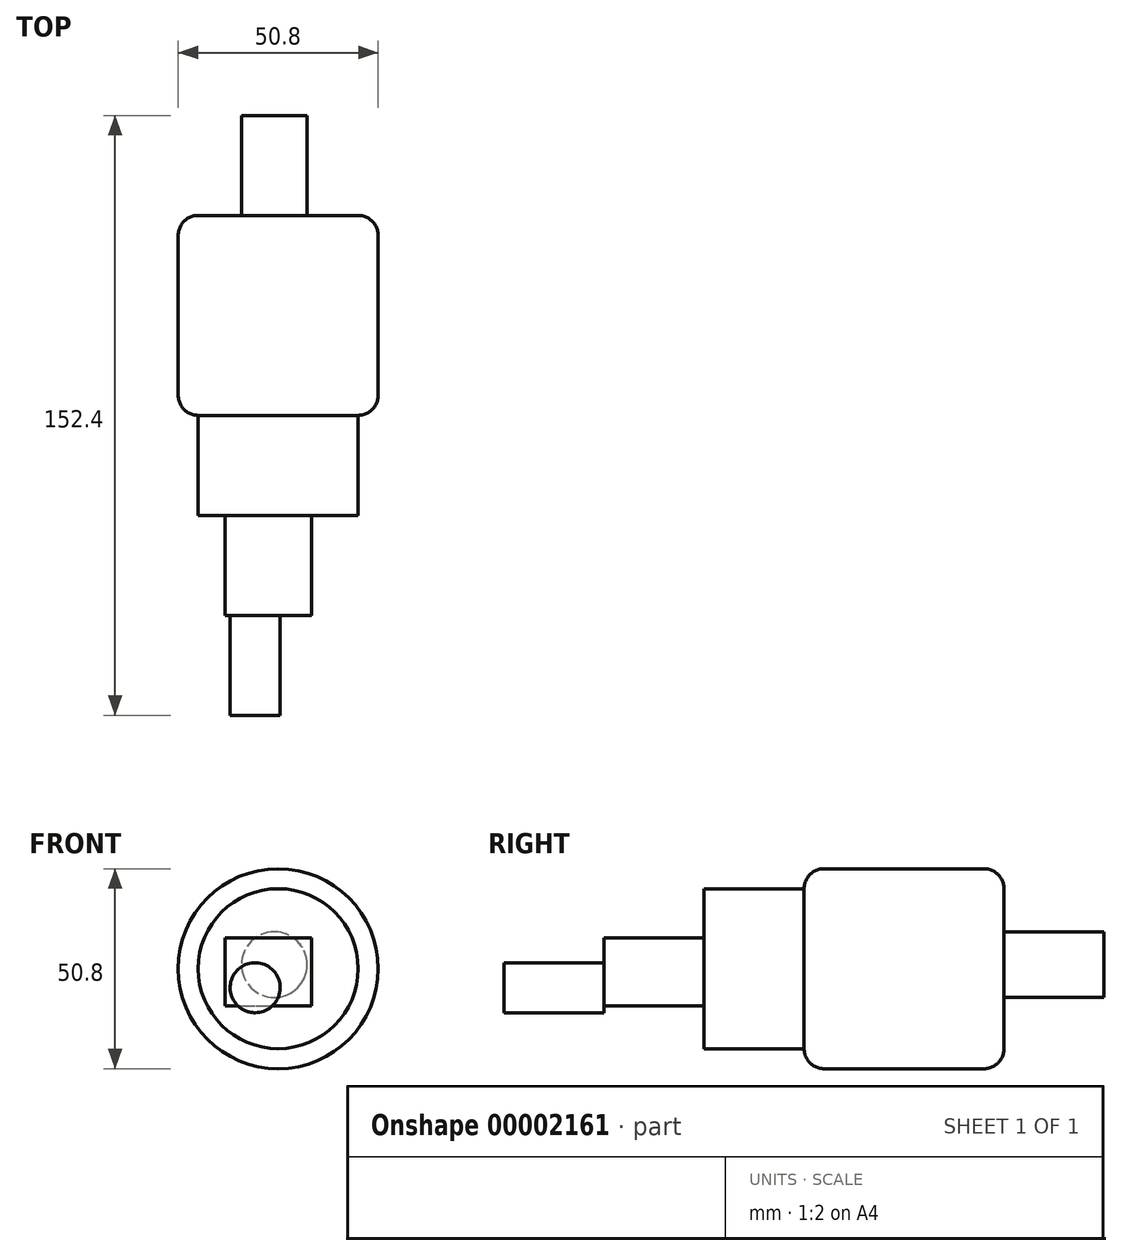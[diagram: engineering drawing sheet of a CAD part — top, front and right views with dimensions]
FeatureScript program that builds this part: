
annotation { "Feature Type Name" : "Feature", "Feature Type Description" : "" }
export const myFeature = defineFeature(function(context is Context, id is Id, definition is map)
    precondition{}
    {
        {
            var Q0;
            Q0=qCreatedBy(makeId("Front.planeOp"),FACE);
            var sketch = newSketch(context, id + "F0", { "sketchPlane" : qUnion([Q0])});
            skCircle(sketch, "E0", {"center": v(-55.14, 59.6) * mm, "radius": 25.4 * mm});
            skSolve(sketch);
        }
        {
            var Q0;
            Q0 = qSketchRegion(id + "F0", true);
            extrude(context, id + "F1", {"entities" : qUnion([Q0]), "depth" : 50.8 * mm});
        }
        {
            var Q0;
            Q0=makeQuery(id+"F1.opExtrude","SWEPT_FACE",FACE,{"disambiguationData":[OSD([sQuery(id+"F0.wireOp",EDGE,"E0")])]});
            fillet(context, id + "F2", {"entities" : qUnion([Q0]), "radius" : 5.08 * mm, "tangentPropagation" : true, "allowEdgeOverflow" : false});
        }
        {
            var Q0;
            Q0=makeQuery(id+"F1.opExtrude","CAP_FACE",FACE,{"disambiguationData":[OSD([sQuery(id+"F0.wireOp",EDGE,"E0")])],"isStart":false});
            extrude(context, id + "F3", {"entities" : qUnion([Q0]), "operationType" : NewBodyOperationType.ADD, "depth" : 25.4 * mm});
        }
        {
            var Q0;
            Q0=makeQuery(id+"F3.opExtrude","CAP_FACE",FACE,{"disambiguationData":[OSD([sQuery(id+"F0.wireOp",EDGE,"E0")])],"isStart":false});
            var sketch = newSketch(context, id + "F4", { "sketchPlane" : qUnion([Q0])});
            skLineSegment(sketch, "E1.bottom", {"start": v(-68.61, 67.47) * mm, "end": v(-46.7, 67.47) * mm});
            skLineSegment(sketch, "E1.top", {"start": v(-68.61, 50.22) * mm, "end": v(-46.7, 50.22) * mm});
            skLineSegment(sketch, "E1.left", {"start": v(-68.61, 67.47) * mm, "end": v(-68.61, 50.22) * mm});
            skLineSegment(sketch, "E1.right", {"start": v(-46.7, 67.47) * mm, "end": v(-46.7, 50.22) * mm});
            skSolve(sketch);
        }
        {
            var Q0;
            Q0=makeQuery(id+"F4.imprint","IMPRINT",FACE,{"disambiguationData":[TD([[makeQuery(id+"F4.imprint","IMPRINT",EDGE,{"derivedFrom":sQuery(id+"F4.wireOp",EDGE,"E1.bottom")}),-1.0]])]});
            var Q1;
            Q1=sQuery(id+"F4.wireOp",EDGE,"E1.top");
            var Q2;
            Q2=sQuery(id+"F4.wireOp",EDGE,"E1.left");
            var Q3;
            Q3=sQuery(id+"F4.wireOp",EDGE,"E1.bottom");
            var Q4;
            Q4=sQuery(id+"F4.wireOp",EDGE,"E1.right");
            extrude(context, id + "F5", {"entities" : qUnion([Q0]), "surfaceEntities" : qUnion([Q1, Q2, Q3, Q4]), "depth" : 25.4 * mm});
        }
        {
            var Q0;
            Q0=makeQuery(id+"F1.opExtrude","CAP_FACE",FACE,{"disambiguationData":[OSD([sQuery(id+"F0.wireOp",EDGE,"E0")])],"isStart":true});
            var sketch = newSketch(context, id + "F6", { "sketchPlane" : qUnion([Q0])});
            skCircle(sketch, "E2", {"center": v(56.1, 60.66) * mm, "radius": 8.35 * mm});
            skSolve(sketch);
        }
        {
            var Q0;
            Q0 = qSketchRegion(id + "F6", true);
            extrude(context, id + "F7", {"entities" : qUnion([Q0]), "operationType" : NewBodyOperationType.ADD, "depth" : 25.4 * mm});
        }
        {
            var Q0;
            Q0=makeQuery(id+"F5.opExtrude","CAP_FACE",FACE,{"disambiguationData":[OSD([sQuery(id+"F4.wireOp",EDGE,"E1.bottom"),sQuery(id+"F4.wireOp",EDGE,"E1.top"),sQuery(id+"F4.wireOp",EDGE,"E1.left"),sQuery(id+"F4.wireOp",EDGE,"E1.right")])],"isStart":false});
            var sketch = newSketch(context, id + "F8", { "sketchPlane" : qUnion([Q0])});
            skCircle(sketch, "E3", {"center": v(-61, 54.77) * mm, "radius": 6.35 * mm});
            skSolve(sketch);
        }
        {
            var Q0;
            Q0 = qSketchRegion(id + "F8", true);
            extrude(context, id + "F9", {"entities" : qUnion([Q0]), "operationType" : NewBodyOperationType.ADD, "depth" : 25.4 * mm});
        }
    });
